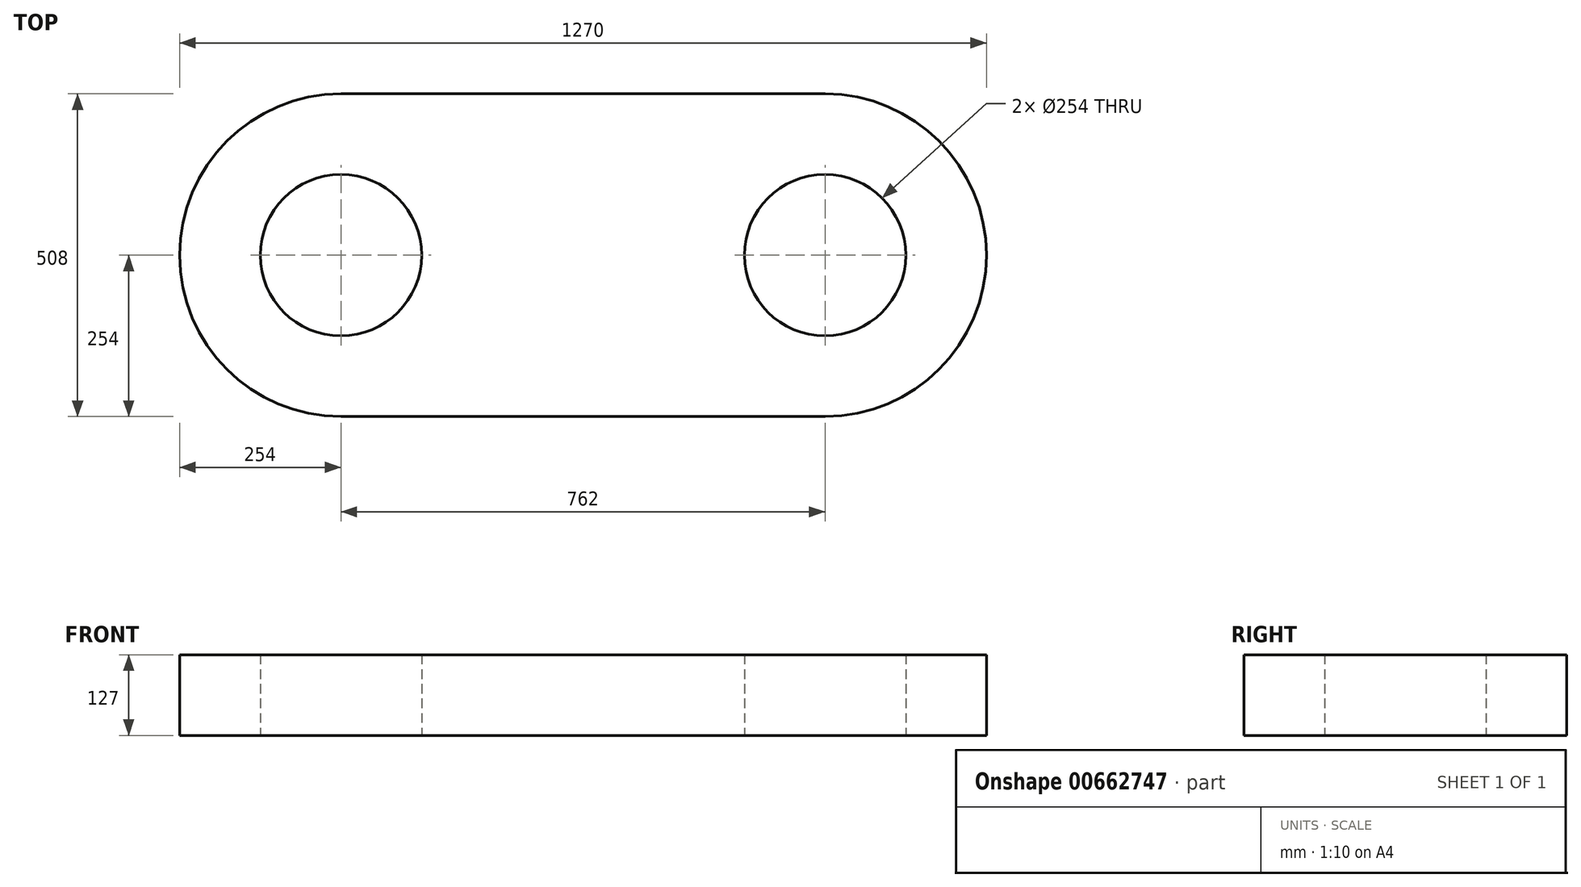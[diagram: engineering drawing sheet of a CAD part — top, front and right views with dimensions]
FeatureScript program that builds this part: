
annotation { "Feature Type Name" : "Feature", "Feature Type Description" : "" }
export const myFeature = defineFeature(function(context is Context, id is Id, definition is map)
    precondition{}
    {
        {
            var Q0;
            Q0=qCreatedBy(makeId("Top.planeOp"),FACE);
            var sketch = newSketch(context, id + "F0", { "sketchPlane" : qUnion([Q0])});
            skLineSegment(sketch, "E0.bottom", {"start": v(-254, 254) * mm, "end": v(508, 254) * mm});
            skLineSegment(sketch, "E0.top", {"start": v(-254, -254) * mm, "end": v(508, -254) * mm});
            skLineSegment(sketch, "E0.left", {"start": v(-254, 254) * mm, "end": v(-254, -254) * mm, "construction": true});
            skLineSegment(sketch, "E0.right", {"start": v(508, 254) * mm, "end": v(508, -254) * mm, "construction": true});
            skArc(sketch, "E1", {"start": v(-254, 254) * mm, "mid": v(-508, 0) * mm, "end": v(-254, -254) * mm});
            skArc(sketch, "E2", {"start": v(508, -254) * mm, "mid": v(762, 0) * mm, "end": v(508, 254) * mm});
            skCircle(sketch, "E3", {"center": v(-254, 0) * mm, "radius": 127 * mm});
            skCircle(sketch, "E4", {"center": v(508, 0) * mm, "radius": 127 * mm});
            skSolve(sketch);
        }
        {
            var Q0;
            Q0 = qSketchRegion(id + "F0", true);
            extrude(context, id + "F1", {"entities" : qUnion([Q0]), "depth" : 127 * mm, "offsetDistance" : 25.4 * mm});
        }
    });
